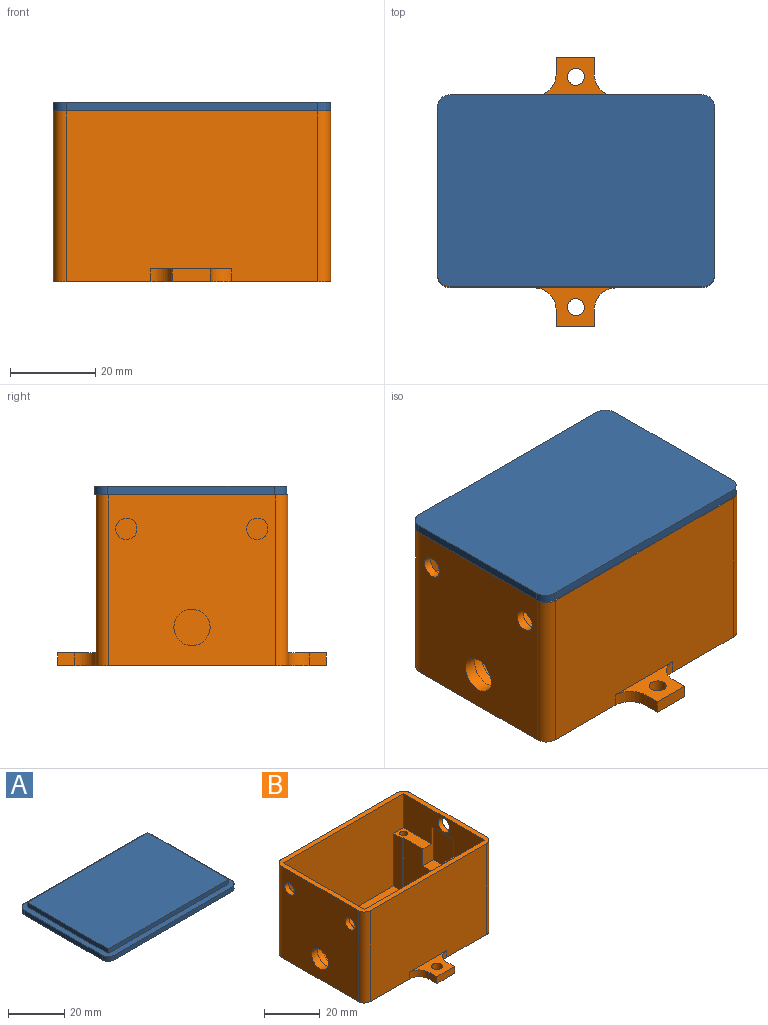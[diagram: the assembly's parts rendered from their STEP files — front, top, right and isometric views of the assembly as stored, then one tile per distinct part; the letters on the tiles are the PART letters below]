
ASSEMBLY  parts=2 mates=1
PART A: 15 faces, bbox 65x45x4 mm
  f0: plane 59x2mm, normal (0,-1,0), area 118mm2, adj f4,f5,f11,f14
  f1: plane 39x2mm, normal (1,0,0), area 78mm2, adj f4,f5,f11,f12
  f2: plane 59x2mm, normal (0,1,0), area 118mm2, adj f4,f5,f12,f13
  f3: plane 39x2mm, normal (-1,0,0), area 78mm2, adj f4,f5,f13,f14
  f4: plane 65x45mm, normal (0,0,1), area 467mm2, adj f0,f1,f2,f3,f7,f8,f9,f10
  f5: plane 65x45mm, normal (0,0,-1), area 2917.3mm2, adj f0,f1,f2,f3,f11,f12,f13,f14
  f6: plane 60.5x40.5mm, normal (0,0,1), area 2450.2mm2, adj f7,f8,f9,f10
  f7: plane 40.5x2mm, normal (-1,0,0), area 81mm2, adj f4,f6,f8,f10
  f8: plane 60.5x2mm, normal (0,-1,0), area 121mm2, adj f4,f6,f7,f9
  f9: plane 40.5x2mm, normal (1,0,0), area 81mm2, adj f4,f6,f8,f10
  f10: plane 60.5x2mm, normal (0,1,0), area 121mm2, adj f4,f6,f7,f9
  f11: cylinder r=3mm len=3mm, axis (0,0,-1), area 9.4mm2, adj f0,f1,f4,f5
  f12: cylinder r=3mm len=3mm, axis (0,0,1), area 9.4mm2, adj f1,f2,f4,f5
  f13: cylinder r=3mm len=3mm, axis (0,0,-1), area 9.4mm2, adj f2,f3,f4,f5
  f14: cylinder r=3mm len=3mm, axis (0,0,1), area 9.4mm2, adj f0,f3,f4,f5
PART B: 61 faces, bbox 65x63x40 mm
  f0: plane 41x6.4mm, normal (0,0,1), area 185.1mm2, adj f2,f3,f4,f12,f13,f14,f21,f23
  f1: plane 14.23x5.15mm, normal (0,0,1), area 60.3mm2, adj f6,f7,f12,f18,f25,f49,f59
  f2: plane 23x1.17mm, normal (0,-1,0), area 26.8mm2, adj f0,f4,f20,f58
  f3: plane 23x1.9mm, normal (0,1,0), area 43.7mm2, adj f0,f4,f20,f56
  f4: plane 32x23mm, normal (1,0,0), area 631.4mm2, adj f0,f2,f3,f20,f54
  f5: cylinder r=4.25mm len=8.5mm, axis (-1,0,0), area 80.1mm2, adj f15,f55
  f6: plane 41x15mm, normal (-1,0,0), area 502.5mm2, adj f1,f8,f12,f13,f16,f49,f50,f53
  f7: plane 32x23mm, normal (-1,0,0), area 651.8mm2, adj f1,f8,f18,f19,f20,f49,f50,f52
  f8: plane 15.55x5.49mm, normal (0,0,1), area 67.8mm2, adj f6,f7,f13,f19,f27,f50,f57
  f9: plane 59x40mm, normal (0,1,0), area 2303mm2, adj f16,f17,f32,f33,f39,f47,f48
  f10: plane 59x40mm, normal (0,-1,0), area 2303mm2, adj f16,f17,f31,f34,f44,f45,f46
  f11: plane 40x39mm, normal (1,0,0), area 1531.7mm2, adj f16,f17,f31,f32,f60
  f12: plane 61x38mm, normal (0,-1,0), area 2069.3mm2, adj f0,f1,f6,f14,f16,f20,f58,f59
  f13: plane 61x38mm, normal (0,1,0), area 2044.4mm2, adj f0,f6,f8,f14,f16,f20,f56,f57
  f14: plane 41x15mm, normal (1,0,0), area 575.7mm2, adj f0,f12,f13,f16,f29,f30
  f15: plane 40x39mm, normal (-1,0,0), area 1464mm2, adj f5,f16,f17,f29,f30,f33,f34
  f16: plane 65x45mm, normal (0,0,1), area 416.3mm2, adj f6,f9,f10,f11,f12,f13,f14,f15
  f17: plane 65x63mm, normal (0,0,-1), area 3075.6mm2, adj f9,f10,f11,f15,f31,f32,f33,f34
  f18: plane 23x0.65mm, normal (0,-1,0), area 14.9mm2, adj f1,f7,f20,f59
  f19: plane 23x0.99mm, normal (0,1,0), area 22.9mm2, adj f7,f8,f20,f57
  f20: plane 52x41mm, normal (0,0,1), area 2110.8mm2, adj f2,f3,f4,f7,f12,f13,f18,f19
  f21: cylinder r=1.45mm len=10mm, axis (0,0,1), area 91.1mm2, adj f0,f22
  f22: plane 2.9x2.9mm, normal (0,0,1), area 6.6mm2, adj f21
  f23: cylinder r=1.45mm len=10mm, axis (0,0,1), area 91.1mm2, adj f0,f24
  f24: plane 2.9x2.9mm, normal (0,0,1), area 6.6mm2, adj f23
  f25: cylinder r=1.45mm len=10mm, axis (0,0,1), area 91.1mm2, adj f1,f26
  f26: plane 2.9x2.9mm, normal (0,0,1), area 6.6mm2, adj f25
  f27: cylinder r=1.45mm len=10mm, axis (0,0,1), area 91.1mm2, adj f8,f28
  f28: plane 2.9x2.9mm, normal (0,0,1), area 6.6mm2, adj f27
  f29: cylinder r=2.5mm len=5mm, axis (-1,0,0), area 31.4mm2, adj f14,f15
  f30: cylinder r=2.5mm len=5mm, axis (-1,0,0), area 31.4mm2, adj f14,f15
  f31: cylinder r=3mm len=40mm, axis (0,0,-1), area 188.5mm2, adj f10,f11,f16,f17
  f32: cylinder r=3mm len=40mm, axis (0,0,1), area 188.5mm2, adj f9,f11,f16,f17
  f33: cylinder r=3mm len=40mm, axis (0,0,-1), area 188.5mm2, adj f9,f15,f16,f17
  f34: cylinder r=3mm len=40mm, axis (0,0,1), area 188.5mm2, adj f10,f15,f16,f17
  f35: plane 4x3mm, normal (1,0,0), area 12mm2, adj f17,f38,f39,f48
  f36: plane 4x3mm, normal (-1,0,0), area 12mm2, adj f17,f38,f39,f47
  f37: cylinder r=2mm len=4mm, axis (0,0,-1), area 37.7mm2, adj f17,f39
  f38: plane 9x3mm, normal (0,1,0), area 27mm2, adj f17,f35,f36,f39
  f39: plane 19x9mm, normal (0,0,1), area 79.2mm2, adj f9,f35,f36,f37,f38,f47,f48
  f40: plane 4x3mm, normal (1,0,0), area 12mm2, adj f17,f41,f44,f45
  f41: plane 9x3mm, normal (0,-1,0), area 27mm2, adj f17,f40,f43,f44
  f42: cylinder r=2mm len=4mm, axis (0,0,-1), area 37.7mm2, adj f17,f44
  f43: plane 4x3mm, normal (-1,0,0), area 12mm2, adj f17,f41,f44,f46
  f44: plane 19x9mm, normal (0,0,1), area 79.2mm2, adj f10,f40,f41,f42,f43,f45,f46
  f45: cylinder r=5mm len=5mm, axis (0,0,1), area 23.6mm2, adj f10,f17,f40,f44
  f46: cylinder r=5mm len=5mm, axis (0,0,-1), area 23.6mm2, adj f10,f17,f43,f44
  f47: cylinder r=5mm len=5mm, axis (0,0,-1), area 23.6mm2, adj f9,f17,f36,f39
  f48: cylinder r=5mm len=5mm, axis (0,0,1), area 23.6mm2, adj f9,f17,f35,f39
  f49: plane 15x5.62mm, normal (0,-1,0), area 50.6mm2, adj f1,f6,f7,f51,f52,f53
  f50: plane 15x5.62mm, normal (0,1,0), area 50.6mm2, adj f6,f7,f8,f51,f52,f53
  f51: plane 15x11.23mm, normal (-1,0,0), area 168.4mm2, adj f49,f50,f52,f53
  f52: plane 11.23x5.62mm, normal (0,0,1), area 63.1mm2, adj f7,f49,f50,f51
  f53: plane 11.23x1.12mm, normal (0,0,-1), area 12.6mm2, adj f6,f49,f50,f51
  f54: cylinder r=5.77mm len=11.54mm, axis (1,0,0), area 126.9mm2, adj f4,f55
  f55: plane 11.54x11.54mm, normal (1,0,0), area 47.8mm2, adj f5,f54
  f56: plane 23x4.5mm, normal (1,0,0), area 103.5mm2, adj f0,f3,f13,f20
  f57: plane 23x4.5mm, normal (-1,0,0), area 103.5mm2, adj f8,f13,f19,f20
  f58: plane 23x4.5mm, normal (1,0,0), area 103.5mm2, adj f0,f2,f12,f20
  f59: plane 23x4.5mm, normal (-1,0,0), area 103.5mm2, adj f1,f12,f18,f20
  f60: cylinder r=3mm len=6mm, axis (1,0,0), area 37.7mm2, adj f6,f11
PLACE A rot(axis=(0,1,0),180deg) t=(-57.81,-10.63,75.16)mm
PLACE B t=(-57.81,-10.88,33.16)mm fixed
MATE fastened B.f16 <-> A.f4  axis (0,0,1) through (-57.81,9.62,73.16)mm
